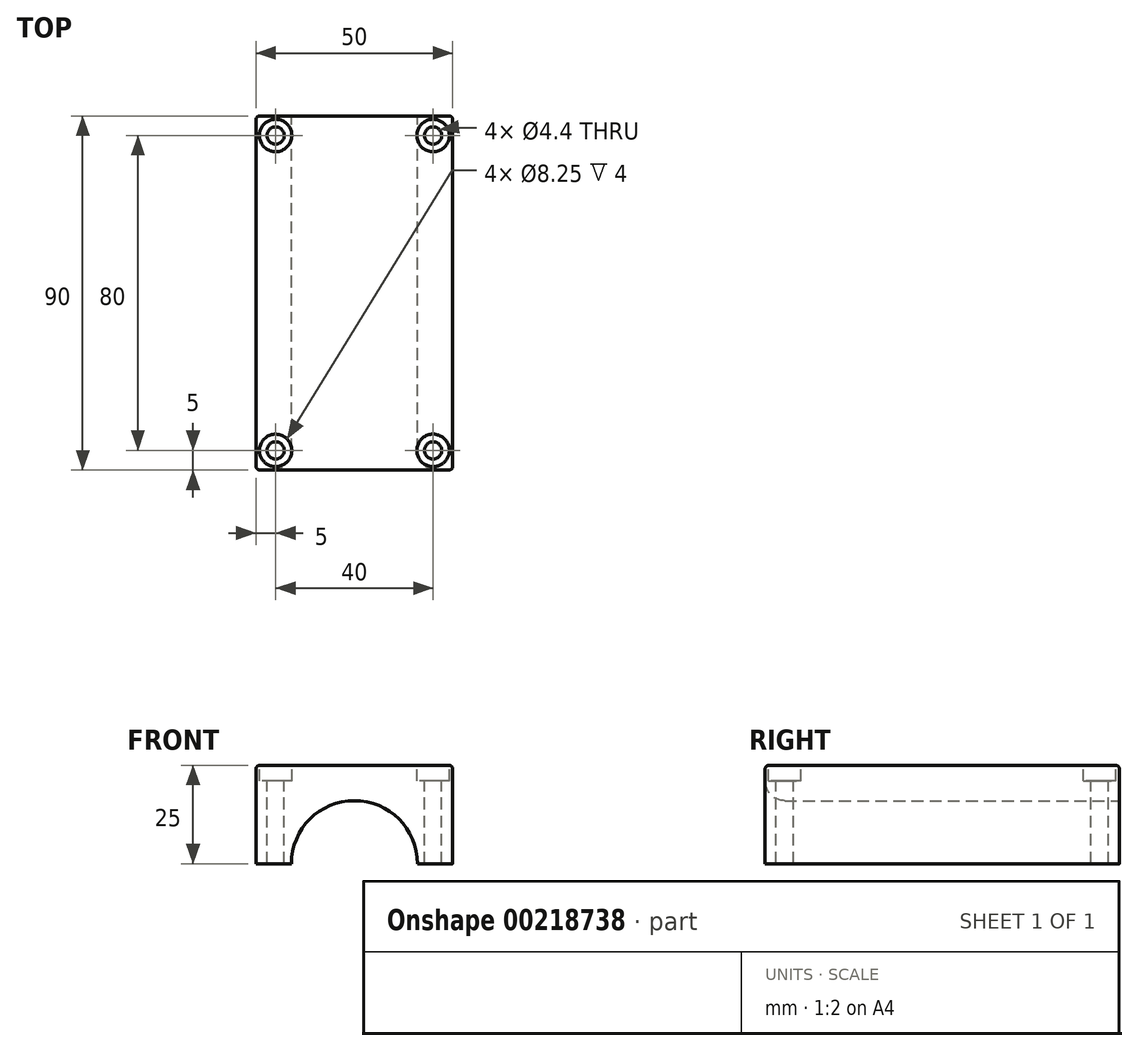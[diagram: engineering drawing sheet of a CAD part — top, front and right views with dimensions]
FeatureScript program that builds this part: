
annotation { "Feature Type Name" : "Feature", "Feature Type Description" : "" }
export const myFeature = defineFeature(function(context is Context, id is Id, definition is map)
    precondition{}
    {
        {
            var Q0;
            Q0=qCreatedBy(makeId("Front.planeOp"),FACE);
            var sketch = newSketch(context, id + "F0", { "sketchPlane" : qUnion([Q0])});
            skLineSegment(sketch, "E0.top", {"start": v(25, 25) * mm, "end": v(-25, 25) * mm});
            skLineSegment(sketch, "E0.left", {"start": v(25, 0) * mm, "end": v(25, 25) * mm});
            skLineSegment(sketch, "E0.right", {"start": v(-25, 0) * mm, "end": v(-25, 25) * mm});
            skPoint(sketch, "E0.middle", {"position": v(0, 0) * mm});
            skArc(sketch, "E1", {"start": v(16, 0) * mm, "mid": v(0, 16) * mm, "end": v(-16, 0) * mm});
            skLineSegment(sketch, "E2", {"start": v(-25, 0) * mm, "end": v(-16, 0) * mm});
            skPoint(sketch, "E3.orphan", {"position": v(25, -25) * mm});
            skPoint(sketch, "E4.orphan", {"position": v(-25, -25) * mm});
            skLineSegment(sketch, "E5.trimOffspring", {"start": v(16, 0) * mm, "end": v(25, 0) * mm});
            skSolve(sketch);
        }
        {
            var Q0;
            Q0=makeQuery(id+"F0.imprint","IMPRINT",FACE,{"disambiguationData":[TD([[makeQuery(id+"F0.imprint","IMPRINT",EDGE,{"derivedFrom":sQuery(id+"F0.wireOp",EDGE,"E0.top")}),1.0]])]});
            extrude(context, id + "F1", {"entities" : qUnion([Q0]), "depth" : 90 * mm});
        }
        {
            var Q0;
            Q0=makeQuery(id+"F1.opExtrude","SWEPT_FACE",FACE,{"disambiguationData":[OSD([sQuery(id+"F0.wireOp",EDGE,"E0.top")])]});
            var sketch = newSketch(context, id + "F2", { "sketchPlane" : qUnion([Q0])});
            skPoint(sketch, "E6", {"position": v(-20, -85) * mm});
            skPoint(sketch, "E7", {"position": v(-20, -5) * mm});
            skPoint(sketch, "E8", {"position": v(20, -5) * mm});
            skPoint(sketch, "E9", {"position": v(20, -85) * mm});
            skSolve(sketch);
        }
        {
            var Q0;
            Q0=sQuery(id+"F2.wireOp",VERTEX,"E6");
            var Q1;
            Q1=sQuery(id+"F2.wireOp",VERTEX,"E7");
            var Q2;
            Q2=sQuery(id+"F2.wireOp",VERTEX,"E8");
            var Q3;
            Q3=sQuery(id+"F2.wireOp",VERTEX,"E9");
            var Q4;
            Q4=makeQuery(id+"F1.opExtrude","SWEPT_BODY",BODY,{"disambiguationData":[OSD([sQuery(id+"F0.wireOp",EDGE,"E0.top"),sQuery(id+"F0.wireOp",EDGE,"E0.left"),sQuery(id+"F0.wireOp",EDGE,"E0.right"),sQuery(id+"F0.wireOp",EDGE,"E1"),sQuery(id+"F0.wireOp",EDGE,"E2"),sQuery(id+"F0.wireOp",EDGE,"E5.trimOffspring")])]});
            hole(context, id + "F3", {"style" : HoleStyle.C_BORE, "endStyle" : HoleEndStyle.THROUGH, "standardTappedOrClearance" : lookupTablePath({ "standard" : "ISO", "fit" : "Normal", "size" : "M4", "type" : "Clearance" }), "standardBlindInLast" : lookupTablePath({ "fit" : "Standard", "standard" : "ISO", "size" : "M4", "type" : "Clearance" }), "holeDiameter" : 4.4 * mm, "cBoreDiameter" : 8.25 * mm, "cBoreDepth" : 4 * mm, "startFromSketch" : true, "locations" : qUnion([Q0, Q1, Q2, Q3]), "scope" : qUnion([Q4]), "isTappedThrough" : true});
        }
        {
            var Q0;
            Q0=makeQuery(id+"F1.opExtrude","CAP_EDGE",EDGE,{"disambiguationData":[OSD([sQuery(id+"F0.wireOp",EDGE,"E1")])],"isStart":false});
            fillet(context, id + "F4", {"entities" : qUnion([Q0]), "radius" : 5 * mm, "tangentPropagation" : true, "allowEdgeOverflow" : false});
        }
        {
            var Q0;
            Q0=makeQuery(id+"F1.opExtrude","SWEPT_EDGE",EDGE,{"disambiguationData":[OSD([sQuery(id+"F0.wireOp",EDGE,"E0.top"),sQuery(id+"F0.wireOp",EDGE,"E0.left")])]});
            var Q1;
            Q1=makeQuery(id+"F1.opExtrude","CAP_EDGE",EDGE,{"disambiguationData":[OSD([sQuery(id+"F0.wireOp",EDGE,"E0.left")])],"isStart":false});
            var Q2;
            Q2=makeQuery(id+"F1.opExtrude","CAP_EDGE",EDGE,{"disambiguationData":[OSD([sQuery(id+"F0.wireOp",EDGE,"E0.top")])],"isStart":true});
            var Q3;
            Q3=makeQuery(id+"F1.opExtrude","SWEPT_EDGE",EDGE,{"disambiguationData":[OSD([sQuery(id+"F0.wireOp",EDGE,"E0.top"),sQuery(id+"F0.wireOp",EDGE,"E0.right")])]});
            var Q4;
            Q4=makeQuery(id+"F1.opExtrude","CAP_EDGE",EDGE,{"disambiguationData":[OSD([sQuery(id+"F0.wireOp",EDGE,"E0.top")])],"isStart":false});
            var Q5;
            Q5=makeQuery(id+"F1.opExtrude","CAP_EDGE",EDGE,{"disambiguationData":[OSD([sQuery(id+"F0.wireOp",EDGE,"E0.left")])],"isStart":true});
            var Q6;
            Q6=makeQuery(id+"F1.opExtrude","CAP_EDGE",EDGE,{"disambiguationData":[OSD([sQuery(id+"F0.wireOp",EDGE,"E0.right")])],"isStart":true});
            var Q7;
            Q7=makeQuery(id+"F1.opExtrude","CAP_EDGE",EDGE,{"disambiguationData":[OSD([sQuery(id+"F0.wireOp",EDGE,"E0.right")])],"isStart":false});
            fillet(context, id + "F5", {"entities" : qUnion([Q0, Q1, Q2, Q3, Q4, Q5, Q6, Q7]), "radius" : 1 * mm, "tangentPropagation" : true, "allowEdgeOverflow" : false});
        }
    });
